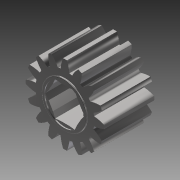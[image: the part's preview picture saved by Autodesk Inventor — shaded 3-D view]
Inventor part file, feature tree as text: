
AUTODESK INVENTOR PART (.ipt)
format: ipt  version: 2014 (Build 180170000, 170)  size: 288,768 bytes
history: native  units: mm (DEFAULTED — no unit token found)
features: sketch x6, plane x5, extrude x4, other x3, mirror x2, pattern_circular x1, fillet x1, revolve x1
ambient origin geometry x8: Origin, YZ Plane, XZ Plane, XY Plane, X Axis, Y Axis, Z Axis, Center Point
bodies: Solid1 (feature_tree)
feature tree (23):
  extrude  "Extrusion1"  Depth=14.605mm TaperAngle=0.0deg
  plane  "Work Plane1"
  plane  "Work Plane2"
  plane  "Work Plane3"
  other  "Spur Gear"
  extrude  "Extrusion2"  Depth=76.2mm TaperAngle=0.0deg
  extrude  "Extrusion3"  TaperAngle=0.0deg  [1 undecoded]
  pattern_circular  "Circular Pattern1"  [2 undecoded]
  extrude  "Extrusion4"  Depth=0.3175mm TaperAngle=0.0deg
  fillet  "Fillet1"  Radius=5.528591mm
  plane  "Work Plane4"
  mirror  "Mirror1"
  plane  "Work Plane5"
  revolve  "Revolution1"  [1 undecoded]
  mirror  "Mirror2"
  sketch  "Sketch1"  dims[d0=22.86mm d1=14.605mm d2=0.0mm]
  sketch  "Sketch2"  dims[d3=20.32mm d4=76.2mm d5=0.0mm]
  other  "Srf1"
  sketch  "Sketch3"  dims[d6=0.0mm d7=1.963495mm d9=0.0mm]
  sketch  "Sketch4"  dims[d14=0.0mm d15=111.76mm]
  sketch  "Sketch5"  dims[d16=0.0mm]
  sketch  "Sketch6"  dims[d17=0.0mm d18=0.0mm d19=111.76mm d20=9.5758mm d21=25.4mm d22=0.0mm d23=5.528591mm d24=1.524mm d25=12.7mm d26=0.0mm d27=60.0mm d28=360.0deg d30=0.3175mm d31=0.0mm d32=0.3175mm d33=30.0deg d34=90.0deg]
  other  "Pitch Diameter"
note: 4 required parameter values undecoded (feature->parameter linkage not recoverable at this tier; creation-order binding heuristic only, values carry confidence <= 0.55)